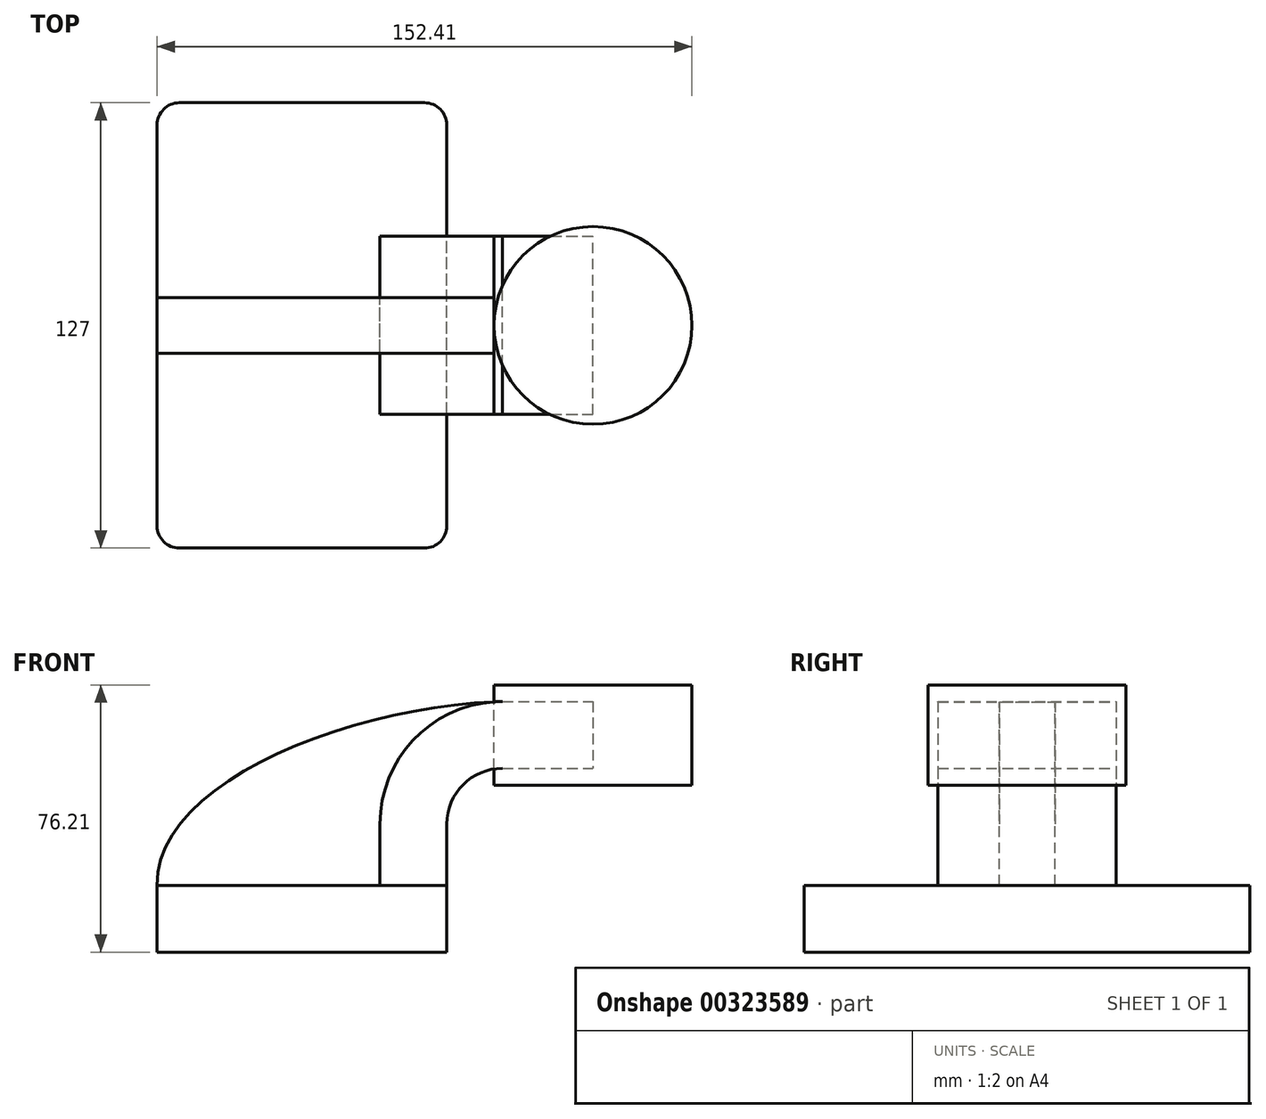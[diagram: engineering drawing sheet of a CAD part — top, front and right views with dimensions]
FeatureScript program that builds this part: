
annotation { "Feature Type Name" : "Feature", "Feature Type Description" : "" }
export const myFeature = defineFeature(function(context is Context, id is Id, definition is map)
    precondition{}
    {
        {
            var Q0;
            Q0=qCreatedBy(makeId("Front.planeOp"),FACE);
            var sketch = newSketch(context, id + "F0", { "sketchPlane" : qUnion([Q0])});
            skLineSegment(sketch, "E0.bottom", {"start": v(41.28, -9.52) * mm, "end": v(-41.28, -9.53) * mm});
            skLineSegment(sketch, "E0.top", {"start": v(41.28, 9.53) * mm, "end": v(-41.28, 9.53) * mm});
            skLineSegment(sketch, "E0.left", {"start": v(41.28, -9.52) * mm, "end": v(41.28, 9.53) * mm});
            skLineSegment(sketch, "E0.right", {"start": v(-41.28, -9.52) * mm, "end": v(-41.28, 9.53) * mm});
            skPoint(sketch, "E0.middle", {"position": v(0, 0) * mm});
            skLineSegment(sketch, "E1.bottom", {"start": v(60.33, 66.68) * mm, "end": v(111.12, 66.68) * mm});
            skLineSegment(sketch, "E1.top", {"start": v(60.33, 38.1) * mm, "end": v(111.12, 38.1) * mm});
            skLineSegment(sketch, "E1.left", {"start": v(60.33, 66.68) * mm, "end": v(60.33, 38.1) * mm});
            skLineSegment(sketch, "E1.right", {"start": v(111.12, 66.68) * mm, "end": v(111.12, 38.1) * mm});
            skPoint(sketch, "E1.middle", {"position": v(85.72, 52.39) * mm});
            skLineSegment(sketch, "E2", {"start": v(41.28, 9.53) * mm, "end": v(41.28, 27) * mm});
            skArc(sketch, "E3", {"start": v(41.27, 27) * mm, "mid": v(45.92, 38.23) * mm, "end": v(57.15, 42.88) * mm});
            skPoint(sketch, "E4.endSnap0", {"position": v(45.92, 38.23) * mm});
            skLineSegment(sketch, "E5", {"start": v(57.15, 42.88) * mm, "end": v(82.93, 42.88) * mm});
            skLineSegment(sketch, "E6.0", {"start": v(57.15, 61.93) * mm, "end": v(82.93, 61.93) * mm});
            skArc(sketch, "E6.1", {"start": v(22.23, 27) * mm, "mid": v(32.45, 51.7) * mm, "end": v(57.15, 61.93) * mm});
            skLineSegment(sketch, "E6.2", {"start": v(22.22, 9.53) * mm, "end": v(22.22, 27) * mm});
            skLineSegment(sketch, "E7", {"start": v(82.93, 61.93) * mm, "end": v(82.93, 42.88) * mm});
            skLineSegment(sketch, "E8", {"start": v(82.93, 61.93) * mm, "end": v(82.93, 66.68) * mm});
            skLineSegment(sketch, "E9", {"start": v(82.93, 42.88) * mm, "end": v(82.93, 38.1) * mm});
            skFitSpline(sketch, "E10", {"points": [v(-41.28, 9.53) * mm, v(57.15, 61.93) * mm], "startDerivative": vector(-1.76, 88.41) * mm, "endDerivative": vector(128.84, 3.29) * mm});
            skSolve(sketch);
        }
        {
            var Q0;
            Q0=makeQuery(id+"F0.imprint","IMPRINT",FACE,{"disambiguationData":[TD([[makeQuery(id+"F0.imprint","IMPRINT",EDGE,{"derivedFrom":sQuery(id+"F0.wireOp",EDGE,"E0.bottom")}),-1.0]])]});
            extrude(context, id + "F1", {"entities" : qUnion([Q0]), "endBound" : BoundingType.SYMMETRIC, "depth" : 127 * mm});
        }
        {
            var Q0;
            {var subQ5=sQuery(id+"F0.wireOp",EDGE,"E7");Q0=makeQuery(id+"F0.imprint","IMPRINT",FACE,{"disambiguationData":[TD([[makeQuery(id+"F0.imprint","IMPRINT",EDGE,{"derivedFrom":subQ5}),-1.0]])]});}
            var Q1;
            {var subQ1=sQuery(id+"F0.wireOp",EDGE,"E2");Q1=makeQuery(id+"F0.imprint","IMPRINT",FACE,{"disambiguationData":[TD([[makeQuery(id+"F0.imprint","IMPRINT",EDGE,{"derivedFrom":subQ1}),1.0]])]});}
            extrude(context, id + "F2", {"entities" : qUnion([Q0, Q1]), "endBound" : BoundingType.SYMMETRIC, "depth" : 50.8 * mm});
        }
        {
            var Q0;
            {var subQ3=sQuery(id+"F0.wireOp",EDGE,"E6.2");Q0=makeQuery(id+"F0.imprint","IMPRINT",FACE,{"disambiguationData":[TD([[makeQuery(id+"F0.imprint","IMPRINT",EDGE,{"derivedFrom":subQ3}),1.0]])]});}
            extrude(context, id + "F3", {"entities" : qUnion([Q0]), "endBound" : BoundingType.SYMMETRIC, "depth" : 15.88 * mm});
        }
        {
            var Q0;
            {var subQ0=sQuery(id+"F0.wireOp",EDGE,"E1.right");Q0=makeQuery(id+"F0.imprint","IMPRINT",FACE,{"disambiguationData":[TD([[makeQuery(id+"F0.imprint","IMPRINT",EDGE,{"derivedFrom":subQ0}),-1.0]])]});}
            var Q1;
            Q1=sQuery(id+"F0.wireOp",EDGE,"E7");
            revolve(context, id + "F4", {"entities" : qUnion([Q0]), "axis" : qUnion([Q1]), "revolveType" : RevolveType.FULL});
        }
        {
            var Q0;
            Q0=makeQuery(id+"F1.opExtrude","CAP_EDGE",EDGE,{"disambiguationData":[OSD([sQuery(id+"F0.wireOp",EDGE,"E0.right")])],"isStart":false});
            var Q1;
            Q1=makeQuery(id+"F1.opExtrude","CAP_EDGE",EDGE,{"disambiguationData":[OSD([sQuery(id+"F0.wireOp",EDGE,"E0.right")])],"isStart":true});
            var Q2;
            Q2=makeQuery(id+"F1.opExtrude","CAP_EDGE",EDGE,{"disambiguationData":[OSD([sQuery(id+"F0.wireOp",EDGE,"E0.left")])],"isStart":true});
            var Q3;
            Q3=makeQuery(id+"F1.opExtrude","CAP_EDGE",EDGE,{"disambiguationData":[OSD([sQuery(id+"F0.wireOp",EDGE,"E0.left")])],"isStart":false});
            fillet(context, id + "F5", {"entities" : qUnion([Q0, Q1, Q2, Q3]), "radius" : 6.35 * mm, "tangentPropagation" : true, "allowEdgeOverflow" : false});
        }
    });
